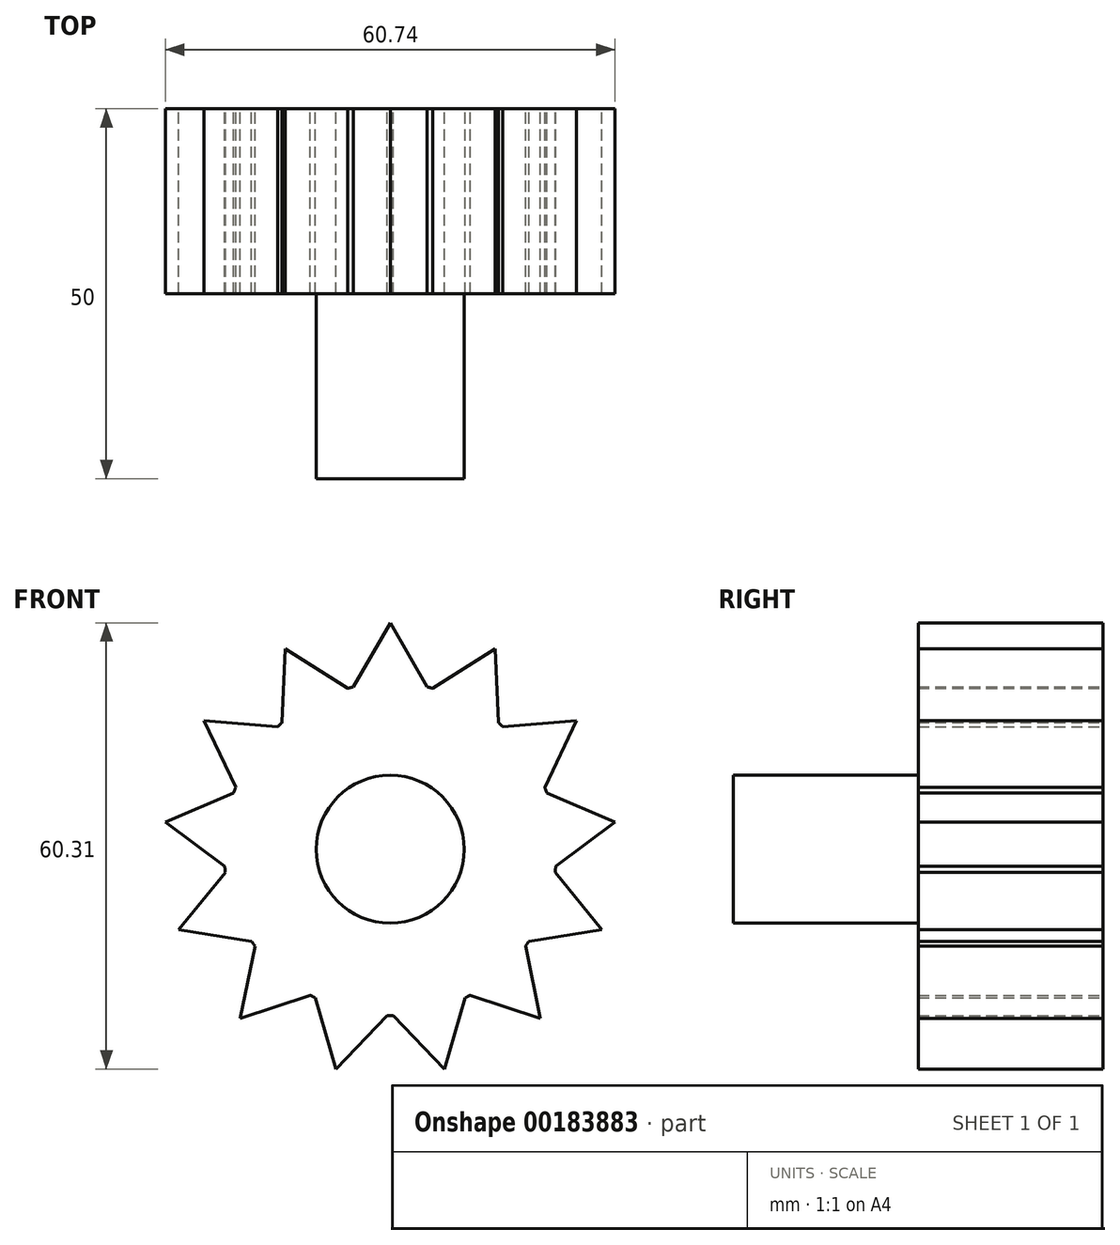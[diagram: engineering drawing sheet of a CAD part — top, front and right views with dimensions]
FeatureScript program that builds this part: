
annotation { "Feature Type Name" : "Feature", "Feature Type Description" : "" }
export const myFeature = defineFeature(function(context is Context, id is Id, definition is map)
    precondition{}
    {
        {
            var Q0;
            Q0=qCreatedBy(makeId("Front.planeOp"),FACE);
            var sketch = newSketch(context, id + "F0", { "sketchPlane" : qUnion([Q0])});
            skCircle(sketch, "E0", {"center": v(0, 0) * mm, "radius": 22.5 * mm});
            skLineSegment(sketch, "E1", {"start": v(-5, 21.94) * mm, "end": v(0, 30.6) * mm});
            skLineSegment(sketch, "E2", {"start": v(0, 30.6) * mm, "end": v(5, 21.94) * mm});
            skLineSegment(sketch, "E3.1.0", {"start": v(-14.22, 27.1) * mm, "end": v(-5.77, 21.75) * mm});
            skLineSegment(sketch, "E3.1.1", {"start": v(-14.62, 17.1) * mm, "end": v(-14.22, 27.1) * mm});
            skLineSegment(sketch, "E3.2.0", {"start": v(-25.18, 17.38) * mm, "end": v(-15.21, 16.58) * mm});
            skLineSegment(sketch, "E3.2.1", {"start": v(-20.9, 8.35) * mm, "end": v(-25.18, 17.38) * mm});
            skLineSegment(sketch, "E3.3.0", {"start": v(-30.37, 3.69) * mm, "end": v(-21.17, 7.6) * mm});
            skLineSegment(sketch, "E3.3.1", {"start": v(-22.38, -2.32) * mm, "end": v(-30.37, 3.69) * mm});
            skLineSegment(sketch, "E3.4.0", {"start": v(-28.6, -10.85) * mm, "end": v(-22.28, -3.1) * mm});
            skLineSegment(sketch, "E3.4.1", {"start": v(-18.74, -12.45) * mm, "end": v(-28.6, -10.85) * mm});
            skLineSegment(sketch, "E3.5.0", {"start": v(-20.3, -22.9) * mm, "end": v(-18.29, -13.1) * mm});
            skLineSegment(sketch, "E3.5.1", {"start": v(-10.8, -19.74) * mm, "end": v(-20.3, -22.9) * mm});
            skLineSegment(sketch, "E3.6.0", {"start": v(-7.32, -29.7) * mm, "end": v(-10.1, -20.1) * mm});
            skLineSegment(sketch, "E3.6.1", {"start": v(-0.4, -22.5) * mm, "end": v(-7.32, -29.7) * mm});
            skLineSegment(sketch, "E3.7.0", {"start": v(7.32, -29.7) * mm, "end": v(0.4, -22.5) * mm});
            skLineSegment(sketch, "E3.7.1", {"start": v(10.1, -20.1) * mm, "end": v(7.32, -29.7) * mm});
            skLineSegment(sketch, "E3.8.0", {"start": v(20.3, -22.9) * mm, "end": v(10.8, -19.74) * mm});
            skLineSegment(sketch, "E3.8.1", {"start": v(18.29, -13.1) * mm, "end": v(20.3, -22.9) * mm});
            skLineSegment(sketch, "E3.9.0", {"start": v(28.6, -10.85) * mm, "end": v(18.74, -12.45) * mm});
            skLineSegment(sketch, "E3.9.1", {"start": v(22.28, -3.1) * mm, "end": v(28.6, -10.85) * mm});
            skLineSegment(sketch, "E3.10.0", {"start": v(30.37, 3.69) * mm, "end": v(22.38, -2.32) * mm});
            skLineSegment(sketch, "E3.10.1", {"start": v(21.17, 7.6) * mm, "end": v(30.37, 3.69) * mm});
            skLineSegment(sketch, "E3.11.0", {"start": v(25.18, 17.38) * mm, "end": v(20.9, 8.35) * mm});
            skLineSegment(sketch, "E3.11.1", {"start": v(15.21, 16.58) * mm, "end": v(25.18, 17.38) * mm});
            skLineSegment(sketch, "E3.12.0", {"start": v(14.22, 27.1) * mm, "end": v(14.62, 17.1) * mm});
            skLineSegment(sketch, "E3.12.1", {"start": v(5.77, 21.75) * mm, "end": v(14.22, 27.1) * mm});
            skSolve(sketch);
        }
        {
            var Q0;
            Q0 = qSketchRegion(id + "F0", true);
            extrude(context, id + "F1", {"entities" : qUnion([Q0]), "depth" : 25 * mm});
        }
        {
            var Q0;
            Q0=makeQuery(id+"F1.opExtrude","CAP_FACE",FACE,{"disambiguationData":[OSD([sQuery(id+"F0.wireOp",EDGE,"E0"),sQuery(id+"F0.wireOp",EDGE,"E1"),sQuery(id+"F0.wireOp",EDGE,"E2"),sQuery(id+"F0.wireOp",EDGE,"E3.1.0"),sQuery(id+"F0.wireOp",EDGE,"E3.1.1"),sQuery(id+"F0.wireOp",EDGE,"E3.2.0"),sQuery(id+"F0.wireOp",EDGE,"E3.2.1"),sQuery(id+"F0.wireOp",EDGE,"E3.3.0"),sQuery(id+"F0.wireOp",EDGE,"E3.3.1"),sQuery(id+"F0.wireOp",EDGE,"E3.4.0"),sQuery(id+"F0.wireOp",EDGE,"E3.4.1"),sQuery(id+"F0.wireOp",EDGE,"E3.5.0"),sQuery(id+"F0.wireOp",EDGE,"E3.5.1"),sQuery(id+"F0.wireOp",EDGE,"E3.6.0"),sQuery(id+"F0.wireOp",EDGE,"E3.6.1"),sQuery(id+"F0.wireOp",EDGE,"E3.7.0"),sQuery(id+"F0.wireOp",EDGE,"E3.7.1"),sQuery(id+"F0.wireOp",EDGE,"E3.8.0"),sQuery(id+"F0.wireOp",EDGE,"E3.8.1"),sQuery(id+"F0.wireOp",EDGE,"E3.9.0"),sQuery(id+"F0.wireOp",EDGE,"E3.9.1"),sQuery(id+"F0.wireOp",EDGE,"E3.10.0"),sQuery(id+"F0.wireOp",EDGE,"E3.10.1"),sQuery(id+"F0.wireOp",EDGE,"E3.11.0"),sQuery(id+"F0.wireOp",EDGE,"E3.11.1"),sQuery(id+"F0.wireOp",EDGE,"E3.12.0"),sQuery(id+"F0.wireOp",EDGE,"E3.12.1")])],"isStart":false});
            var sketch = newSketch(context, id + "F2", { "sketchPlane" : qUnion([Q0])});
            skCircle(sketch, "E4", {"center": v(0, 0) * mm, "radius": 10 * mm});
            skSolve(sketch);
        }
        {
            var Q0;
            Q0 = qSketchRegion(id + "F2", true);
            extrude(context, id + "F3", {"entities" : qUnion([Q0]), "operationType" : NewBodyOperationType.ADD, "depth" : 25 * mm});
        }
    });
